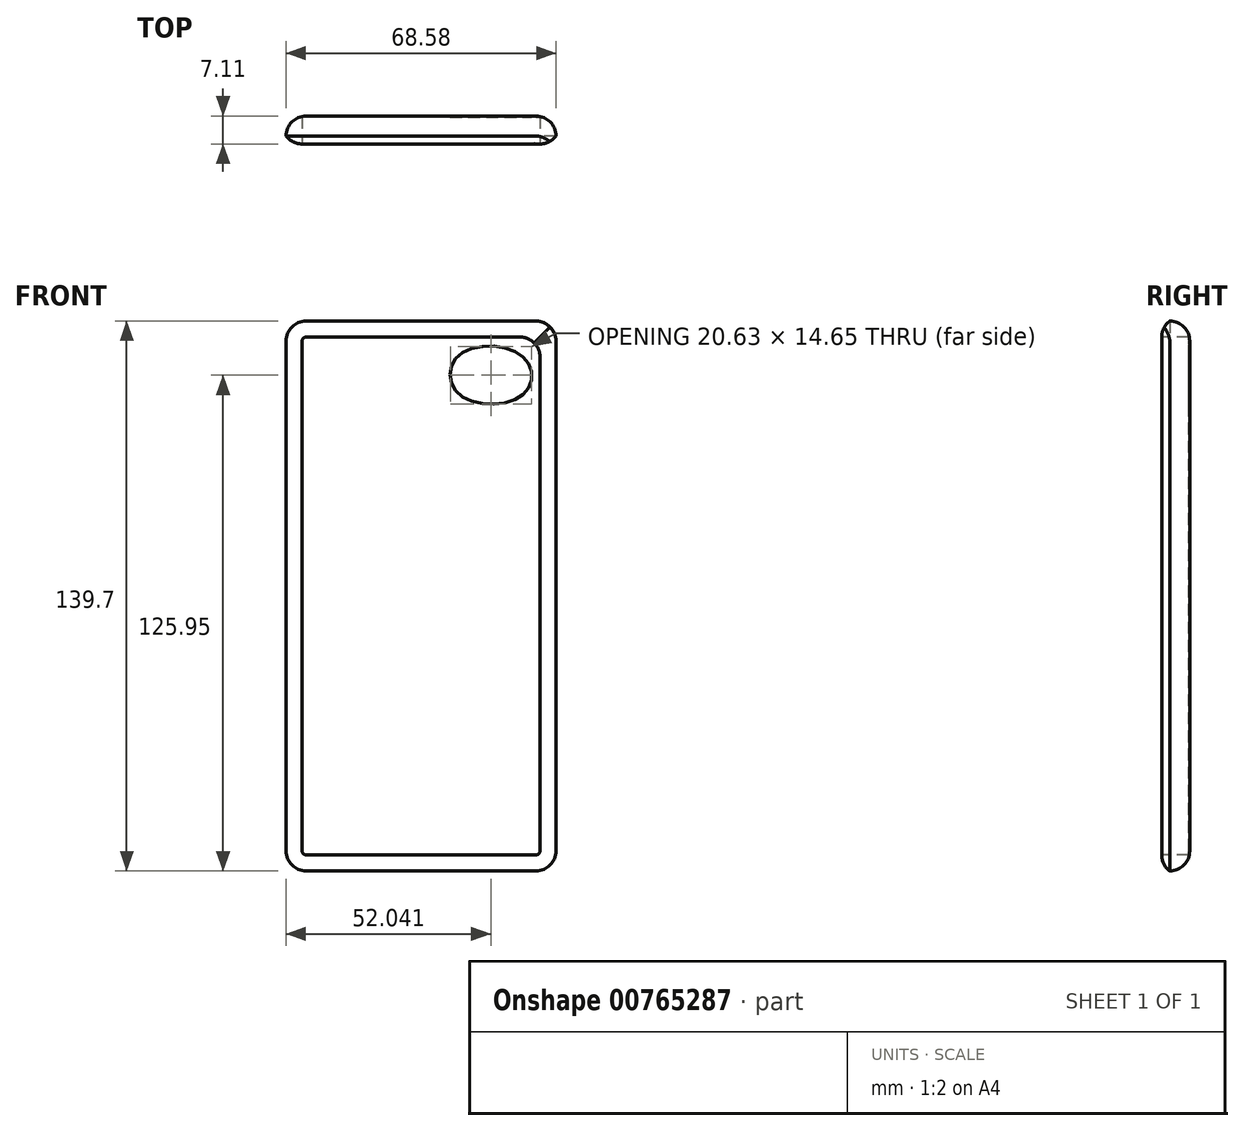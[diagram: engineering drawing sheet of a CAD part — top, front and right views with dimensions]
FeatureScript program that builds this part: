
annotation { "Feature Type Name" : "Feature", "Feature Type Description" : "" }
export const myFeature = defineFeature(function(context is Context, id is Id, definition is map)
    precondition{}
    {
        {
            var Q0;
            Q0=qCreatedBy(makeId("Front.planeOp"),FACE);
            var sketch = newSketch(context, id + "F0", { "sketchPlane" : qUnion([Q0])});
            skLineSegment(sketch, "E0.bottom", {"start": v(-39.54, 76.2) * mm, "end": v(29.04, 76.2) * mm});
            skLineSegment(sketch, "E0.top", {"start": v(-39.54, -63.5) * mm, "end": v(29.04, -63.5) * mm});
            skLineSegment(sketch, "E0.left", {"start": v(-39.54, 76.2) * mm, "end": v(-39.54, -63.5) * mm});
            skLineSegment(sketch, "E0.right", {"start": v(29.04, 76.2) * mm, "end": v(29.04, -63.5) * mm});
            skSolve(sketch);
        }
        {
            var Q0;
            Q0 = qSketchRegion(id + "F0", true);
            extrude(context, id + "F1", {"entities" : qUnion([Q0]), "depth" : 7.11 * mm, "offsetDistance" : 25.4 * mm});
        }
        {
            var Q0;
            Q0=makeQuery(id+"F1.opExtrude","CAP_EDGE",EDGE,{"disambiguationData":[OSD([sQuery(id+"F0.wireOp",EDGE,"E0.right")])],"isStart":true});
            var Q1;
            Q1=makeQuery(id+"F1.opExtrude","CAP_EDGE",EDGE,{"disambiguationData":[OSD([sQuery(id+"F0.wireOp",EDGE,"E0.bottom")])],"isStart":true});
            fillet(context, id + "F2", {"entities" : qUnion([Q0, Q1]), "radius" : 5.08 * mm, "tangentPropagation" : true, "allowEdgeOverflow" : false});
        }
        {
            var Q0;
            {var subQ0=sQuery(id+"F0.wireOp",EDGE,"E0.bottom");Q0=makeQuery(id+"F2.opFillet","BLEND_EDGE",EDGE,{"blendedFrom":[makeQuery(id+"F1.opExtrude","CAP_EDGE",EDGE,{"disambiguationData":[OSD([subQ0])],"isStart":true}),makeQuery(id+"F1.opExtrude","CAP_FACE",FACE,{"disambiguationData":[OSD([subQ0,sQuery(id+"F0.wireOp",EDGE,"E0.top"),sQuery(id+"F0.wireOp",EDGE,"E0.left"),sQuery(id+"F0.wireOp",EDGE,"E0.right")])],"isStart":true})],"blendedInto":[makeQuery(id+"F1.opExtrude","CAP_FACE",FACE,{"disambiguationData":[OSD([subQ0,sQuery(id+"F0.wireOp",EDGE,"E0.top"),sQuery(id+"F0.wireOp",EDGE,"E0.left"),sQuery(id+"F0.wireOp",EDGE,"E0.right")])],"isStart":true})]});}
            var Q1;
            Q1=makeQuery(id+"F1.opExtrude","CAP_EDGE",EDGE,{"disambiguationData":[OSD([sQuery(id+"F0.wireOp",EDGE,"E0.left")])],"isStart":true});
            fillet(context, id + "F3", {"entities" : qUnion([Q0, Q1]), "radius" : 5.08 * mm, "tangentPropagation" : true, "allowEdgeOverflow" : false});
        }
        {
            var Q0;
            Q0=makeQuery(id+"F1.opExtrude","CAP_EDGE",EDGE,{"disambiguationData":[OSD([sQuery(id+"F0.wireOp",EDGE,"E0.top")])],"isStart":true});
            var Q1;
            {var subQ0=sQuery(id+"F0.wireOp",EDGE,"E0.left");Q1=makeQuery(id+"F3.opFillet","BLEND_EDGE",EDGE,{"blendedFrom":[makeQuery(id+"F1.opExtrude","CAP_EDGE",EDGE,{"disambiguationData":[OSD([subQ0])],"isStart":true}),makeQuery(id+"F1.opExtrude","CAP_FACE",FACE,{"disambiguationData":[OSD([sQuery(id+"F0.wireOp",EDGE,"E0.bottom"),sQuery(id+"F0.wireOp",EDGE,"E0.top"),subQ0,sQuery(id+"F0.wireOp",EDGE,"E0.right")])],"isStart":true})],"blendedInto":[makeQuery(id+"F1.opExtrude","CAP_FACE",FACE,{"disambiguationData":[OSD([sQuery(id+"F0.wireOp",EDGE,"E0.bottom"),sQuery(id+"F0.wireOp",EDGE,"E0.top"),subQ0,sQuery(id+"F0.wireOp",EDGE,"E0.right")])],"isStart":true})]});}
            fillet(context, id + "F4", {"entities" : qUnion([Q0, Q1]), "radius" : 5.08 * mm, "tangentPropagation" : true, "allowEdgeOverflow" : false});
        }
        {
            var Q0;
            Q0=makeQuery(id+"F1.opExtrude","CAP_EDGE",EDGE,{"disambiguationData":[OSD([sQuery(id+"F0.wireOp",EDGE,"E0.bottom")])],"isStart":false});
            var Q1;
            Q1=makeQuery(id+"F1.opExtrude","CAP_EDGE",EDGE,{"disambiguationData":[OSD([sQuery(id+"F0.wireOp",EDGE,"E0.right")])],"isStart":false});
            fillet(context, id + "F5", {"entities" : qUnion([Q0, Q1]), "radius" : 5.08 * mm, "tangentPropagation" : true, "allowEdgeOverflow" : false});
        }
        {
            var Q0;
            Q0=makeQuery(id+"F2.opFillet","BLEND_EDGE",EDGE,{"blendedFrom":[makeQuery(id+"F1.opExtrude","CAP_EDGE",EDGE,{"disambiguationData":[OSD([sQuery(id+"F0.wireOp",EDGE,"E0.bottom")])],"isStart":true}),makeQuery(id+"F1.opExtrude","CAP_EDGE",EDGE,{"disambiguationData":[OSD([sQuery(id+"F0.wireOp",EDGE,"E0.right")])],"isStart":true})],"blendedInto":[]});
            fillet(context, id + "F6", {"entities" : qUnion([Q0]), "radius" : 5.08 * mm, "tangentPropagation" : true, "allowEdgeOverflow" : false});
        }
        {
            var Q0;
            Q0=makeQuery(id+"F1.opExtrude","CAP_FACE",FACE,{"disambiguationData":[OSD([sQuery(id+"F0.wireOp",EDGE,"E0.bottom"),sQuery(id+"F0.wireOp",EDGE,"E0.top"),sQuery(id+"F0.wireOp",EDGE,"E0.left"),sQuery(id+"F0.wireOp",EDGE,"E0.right")])],"isStart":false});
            extrude(context, id + "F7", {"entities" : qUnion([Q0]), "operationType" : NewBodyOperationType.REMOVE, "oppositeDirection" : true, "depth" : 6.86 * mm, "offsetDistance" : 25.4 * mm});
        }
        {
            var Q0;
            {var subQ0=sQuery(id+"F0.wireOp",EDGE,"E0.right");var subQ1=sQuery(id+"F0.wireOp",EDGE,"E0.left");var subQ2=sQuery(id+"F0.wireOp",EDGE,"E0.top");var subQ3=sQuery(id+"F0.wireOp",EDGE,"E0.bottom");Q0=makeQuery(id+"F7.boolean.opBoolean","COPY",EDGE,{"derivedFrom":makeQuery(id+"F7.opExtrude","SWEPT_EDGE",EDGE,{"disambiguationData":[OSD([subQ3,subQ2,subQ1,subQ0]),TDD([makeQuery(id+"F5.opFillet","BLEND_VERTEX",VERTEX,{"blendedFrom":[makeQuery(id+"F1.opExtrude","CAP_EDGE",EDGE,{"disambiguationData":[OSD([subQ3])],"isStart":false}),makeQuery(id+"F1.opExtrude","CAP_EDGE",EDGE,{"disambiguationData":[OSD([subQ0])],"isStart":false}),makeQuery(id+"F1.opExtrude","CAP_FACE",FACE,{"disambiguationData":[OSD([subQ3,subQ2,subQ1,subQ0])],"isStart":false})],"blendedInto":[makeQuery(id+"F1.opExtrude","CAP_FACE",FACE,{"disambiguationData":[OSD([subQ3,subQ2,subQ1,subQ0])],"isStart":false})]})])]})});}
            fillet(context, id + "F8", {"entities" : qUnion([Q0]), "radius" : 5.08 * mm, "tangentPropagation" : true, "allowEdgeOverflow" : false});
        }
        {
            var Q0;
            Q0=makeQuery(id+"F1.opExtrude","CAP_FACE",FACE,{"disambiguationData":[OSD([sQuery(id+"F0.wireOp",EDGE,"E0.bottom"),sQuery(id+"F0.wireOp",EDGE,"E0.top"),sQuery(id+"F0.wireOp",EDGE,"E0.left"),sQuery(id+"F0.wireOp",EDGE,"E0.right")])],"isStart":true});
            var sketch = newSketch(context, id + "F9", { "sketchPlane" : qUnion([Q0])});
            skFitSpline(sketch, "E1", {"points": [v(-20.7, 67.13) * mm, v(-20.7, 57.58) * mm, v(-4.47, 57.58) * mm, v(-4.28, 67.51) * mm, v(-20.7, 67.13) * mm]});
            skSolve(sketch);
        }
        {
            var Q0;
            Q0 = qSketchRegion(id + "F9", true);
            extrude(context, id + "F10", {"entities" : qUnion([Q0]), "operationType" : NewBodyOperationType.REMOVE, "oppositeDirection" : true, "depth" : 25.4 * mm, "offsetDistance" : 25.4 * mm});
        }
    });
